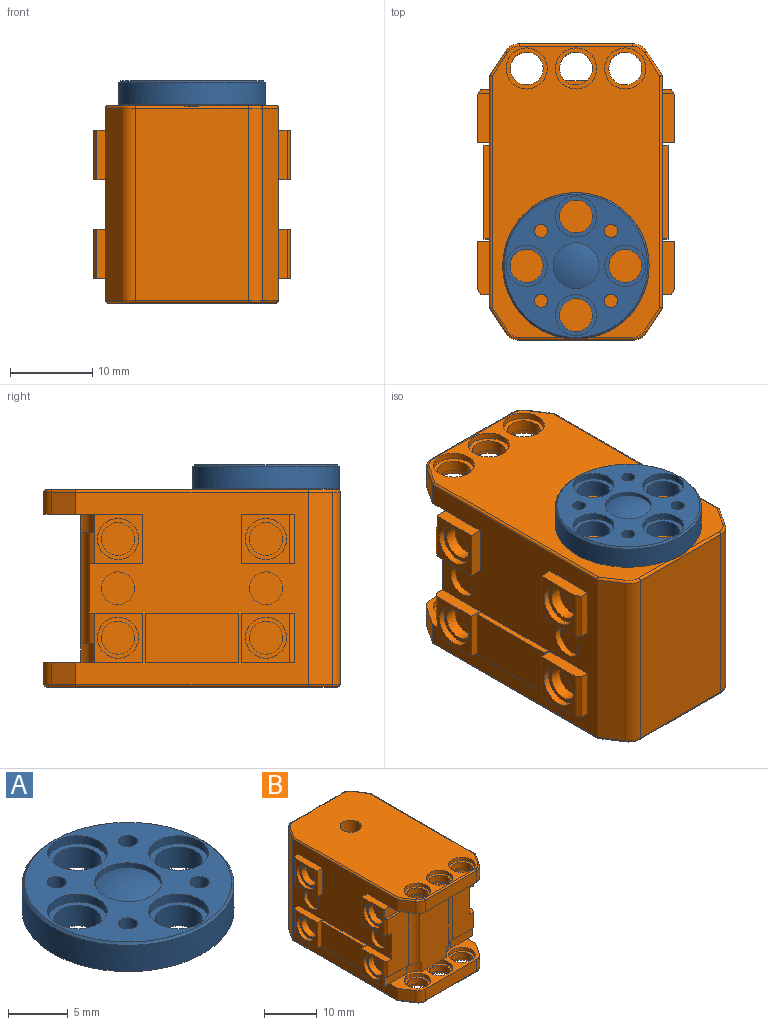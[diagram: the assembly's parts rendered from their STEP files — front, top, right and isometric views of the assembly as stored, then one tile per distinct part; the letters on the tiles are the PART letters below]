
ASSEMBLY  parts=2 mates=1
PART A: 22 faces, bbox 17.8x17.8x2.9 mm
  f0: revolved ~5.62x5.6mm, area 25.4mm2, adj f13
  f1: plane 5x5mm, normal (0,0,1), area 7.1mm2, adj f2,f3
  f2: cylinder r=2mm len=4mm, axis (0,0,1), area 26.4mm2, adj f1,f21
  f3: cylinder r=2.5mm len=5mm, axis (0,0,1), area 12.6mm2, adj f1,f19
  f4: plane 5x5mm, normal (0,0,1), area 7.1mm2, adj f5,f6
  f5: cylinder r=2mm len=4mm, axis (0,0,1), area 26.4mm2, adj f4,f21
  f6: cylinder r=2.5mm len=5mm, axis (0,0,1), area 12.6mm2, adj f4,f19
  f7: plane 5x5mm, normal (0,0,1), area 7.1mm2, adj f8,f9
  f8: cylinder r=2mm len=4mm, axis (0,0,1), area 26.4mm2, adj f7,f21
  f9: cylinder r=2.5mm len=5mm, axis (0,0,1), area 12.6mm2, adj f7,f19
  f10: plane 5x5mm, normal (0,0,1), area 7.1mm2, adj f11,f12
  f11: cylinder r=2mm len=4mm, axis (0,0,1), area 26.4mm2, adj f10,f21
  f12: cylinder r=2.5mm len=5mm, axis (0,0,1), area 12.6mm2, adj f10,f19
  f13: cylinder r=2.8mm len=5.6mm, axis (0,0,1), area 8.8mm2, adj f0,f19
  f14: cone r=8.9mm half-angle=45deg, axis (0,0,-1), area 15.6mm2, adj f15,f19
  f15: cylinder r=8.9mm len=17.8mm, axis (0,0,1), area 151mm2, adj f14,f21
  f16: cylinder r=0.8mm len=2.9mm, axis (0,0,1), area 14.6mm2, adj f19,f21
  f17: cylinder r=0.8mm len=2.9mm, axis (0,0,1), area 14.6mm2, adj f19,f21
  f18: cylinder r=0.8mm len=2.9mm, axis (0,0,1), area 14.6mm2, adj f19,f21
  f19: plane 17.4x17.4mm, normal (0,0,1), area 126.6mm2, adj f3,f6,f9,f12,f13,f14,f16,f17
  f20: cylinder r=0.8mm len=2.9mm, axis (0,0,1), area 14.6mm2, adj f19,f21
  f21: plane 17.8x17.8mm, normal (0,0,-1), area 190.5mm2, adj f2,f5,f8,f11,f15,f16,f17,f18
PART B: 203 faces, bbox 24x36x24 mm
  f0: cylinder r=8.9mm len=3.75mm, axis (0,0,1), area 0mm2, adj f1,f138
  f1: plane 35.6x20.4mm, normal (0,0,1), area 633.5mm2, adj f0,f38,f39,f40,f42,f43,f44,f61
  f2: plane 4x4mm, normal (1,0,0), area 12.6mm2, adj f10
  f3: plane 4x4mm, normal (1,0,0), area 12.6mm2, adj f11
  f4: plane 4x4mm, normal (1,0,0), area 12.6mm2, adj f12
  f5: plane 4x4mm, normal (1,0,0), area 12.6mm2, adj f13
  f6: plane 4x4mm, normal (-1,0,0), area 12.6mm2, adj f14
  f7: plane 4x4mm, normal (-1,0,0), area 12.6mm2, adj f15
  f8: plane 4x4mm, normal (-1,0,0), area 12.6mm2, adj f16
  f9: plane 4x4mm, normal (-1,0,0), area 12.6mm2, adj f17
  f10: cylinder r=2mm len=4mm, axis (1,0,0), area 17.6mm2, adj f2,f18
  f11: cylinder r=2mm len=4mm, axis (1,0,0), area 17.6mm2, adj f3,f19
  f12: cylinder r=2mm len=4mm, axis (1,0,0), area 17.6mm2, adj f4,f20
  f13: cylinder r=2mm len=4mm, axis (1,0,0), area 17.6mm2, adj f5,f21
  f14: cylinder r=2mm len=4mm, axis (1,0,0), area 17.6mm2, adj f6,f28
  f15: cylinder r=2mm len=4mm, axis (1,0,0), area 17.6mm2, adj f7,f29
  f16: cylinder r=2mm len=4mm, axis (1,0,0), area 17.6mm2, adj f8,f31
  f17: cylinder r=2mm len=4mm, axis (1,0,0), area 17.6mm2, adj f9,f32
  f18: plane 5x5mm, normal (1,0,0), area 7.1mm2, adj f10,f34
  f19: plane 5x5mm, normal (1,0,0), area 7.1mm2, adj f11,f35
  f20: plane 5x5mm, normal (1,0,0), area 7.1mm2, adj f12,f36
  f21: plane 5x5mm, normal (1,0,0), area 7.1mm2, adj f13,f37
  f22: plane 5x5mm, normal (0,0,1), area 7.1mm2, adj f26,f38
  f23: plane 5x5mm, normal (0,0,1), area 7.1mm2, adj f25,f39
  f24: plane 5x5mm, normal (0,0,1), area 7.1mm2, adj f27,f40
  f25: cylinder r=2mm len=4mm, axis (0,0,1), area 17.6mm2, adj f23,f41
  f26: cylinder r=2mm len=4mm, axis (0,0,1), area 17.6mm2, adj f22,f45
  f27: cylinder r=2mm len=4mm, axis (0,0,1), area 17.6mm2, adj f24,f46
  f28: plane 5x5mm, normal (-1,0,0), area 7.1mm2, adj f14,f47
  f29: plane 5x5mm, normal (-1,0,0), area 7.1mm2, adj f15,f48
  f30: plane 4x1mm, normal (0,0,1), area 2.8mm2, adj f49,f74
  f31: plane 5x5mm, normal (-1,0,0), area 7.1mm2, adj f16,f50
  f32: plane 5x5mm, normal (-1,0,0), area 7.1mm2, adj f17,f51
  f33: plane 4x1mm, normal (0,0,-1), area 2.8mm2, adj f49,f91
  f34: cylinder r=2.5mm len=5mm, axis (1,0,0), area 12.6mm2, adj f18,f54
  f35: cylinder r=2.5mm len=5mm, axis (1,0,0), area 12.6mm2, adj f19,f60
  f36: cylinder r=2.5mm len=5mm, axis (1,0,0), area 12.6mm2, adj f20,f63
  f37: cylinder r=2.5mm len=5mm, axis (1,0,0), area 12.6mm2, adj f21,f65
  f38: cylinder r=2.5mm len=5mm, axis (0,0,1), area 12.6mm2, adj f1,f22
  f39: cylinder r=2.5mm len=5mm, axis (0,0,1), area 12.6mm2, adj f1,f23
  f40: cylinder r=2.5mm len=5mm, axis (0,0,1), area 12.6mm2, adj f1,f24
  f41: plane 5x5mm, normal (0,0,-1), area 7.1mm2, adj f25,f74
  f42: revolved ~1.68x1.07mm, area 0.9mm2, adj f1,f43,f73,f77
  f43: cylinder r=0.3mm len=13.83mm, axis (1,0,0), area 6.5mm2, adj f1,f42,f44,f78
  f44: revolved ~1.68x1.07mm, area 0.9mm2, adj f1,f43,f61,f79
  f45: plane 5x5mm, normal (0,0,-1), area 7.1mm2, adj f26,f82
  f46: plane 5x5mm, normal (0,0,-1), area 7.1mm2, adj f27,f83
  f47: cylinder r=2.5mm len=5mm, axis (1,0,0), area 12.6mm2, adj f28,f84
  f48: cylinder r=2.5mm len=5mm, axis (1,0,0), area 12.6mm2, adj f29,f90
  f49: plane 18x8mm, normal (0,-1,0), area 138.4mm2, adj f30,f33,f56,f57,f58,f75,f81,f86
  f50: cylinder r=2.5mm len=5mm, axis (1,0,0), area 12.6mm2, adj f31,f99
  f51: cylinder r=2.5mm len=5mm, axis (1,0,0), area 12.6mm2, adj f32,f101
  f52: revolved ~1.68x1.07mm, area 0.9mm2, adj f111,f186,f187,f200
  f53: revolved ~1.68x1.07mm, area 0.9mm2, adj f112,f187,f188,f200
  f54: plane 6x5.84mm, normal (1,0,0), area 15.4mm2, adj f34,f59,f114,f115,f116
  f55: plane 6x0.66mm, normal (0.84,-0.54,0), area 3.3mm2, adj f56,f60,f80,f117,f118,f120
  f56: plane 8.54x1.53mm, normal (0,0,1), area 4.5mm2, adj f49,f55,f57,f80,f81,f117
  f57: cylinder r=2.5mm len=13.5mm, axis (0,0,1), area 31.3mm2, adj f49,f56,f58,f117
  f58: plane 8.54x1.53mm, normal (0,0,-1), area 4.5mm2, adj f49,f57,f59,f94,f95,f117
  f59: plane 6x0.66mm, normal (0.84,-0.54,0), area 3.3mm2, adj f54,f58,f94,f114,f116,f117
  f60: plane 6x5.84mm, normal (1,0,0), area 15.4mm2, adj f35,f55,f118,f119,f120
  f61: cylinder r=0.3mm len=3.1mm, axis (0.54,0.84,0), area 1.6mm2, adj f1,f44,f113,f121
  f62: plane 6x0.66mm, normal (0.84,0.54,0), area 4.7mm2, adj f63,f122,f123,f124
  f63: plane 6x5.84mm, normal (1,0,0), area 15.4mm2, adj f36,f62,f122,f124,f125
  f64: plane 6x0.66mm, normal (0.84,0.54,0), area 4.7mm2, adj f65,f126,f127,f128
  f65: plane 6x5.84mm, normal (1,0,0), area 15.4mm2, adj f37,f64,f126,f128,f129
  f66: plane 4x4mm, normal (1,0,0), area 12.6mm2, adj f130
  f67: plane 4x4mm, normal (1,0,0), area 12.6mm2, adj f131
  f68: plane 11.4x6mm, normal (1,0,0), area 68.4mm2, adj f132,f133,f134,f135
  f69: revolved ~1.68x1.07mm, area 0.9mm2, adj f137,f190,f191,f200
  f70: revolved ~1.68x1.07mm, area 0.9mm2, adj f1,f136,f137,f138
  f71: revolved ~1.68x1.07mm, area 0.9mm2, adj f139,f191,f192,f200
  f72: revolved ~1.68x1.07mm, area 0.9mm2, adj f1,f138,f139,f140
  f73: cylinder r=0.3mm len=3.1mm, axis (0.54,-0.84,0), area 1.6mm2, adj f1,f42,f141,f142
  f74: cylinder r=2.5mm len=5mm, axis (0,0,1), area 12.6mm2, adj f30,f41,f143
  f75: cylinder r=3.02mm len=2.63mm, axis (0,0,1), area 7.2mm2, adj f49,f76,f88,f143
  f76: plane 5.91x2.25mm, normal (0,-1,0), area 13.3mm2, adj f75,f88,f89,f143,f144
  f77: cylinder r=2mm len=2.7mm, axis (0,0,1), area 5.4mm2, adj f42,f78,f142,f143
  f78: plane 13.83x2.7mm, normal (0,-1,0), area 37.3mm2, adj f43,f77,f79,f143
  f79: cylinder r=2mm len=2.7mm, axis (0,0,1), area 5.4mm2, adj f44,f78,f121,f143
  f80: plane 5.91x2.25mm, normal (0,-1,0), area 13.3mm2, adj f55,f56,f81,f120,f143
  f81: cylinder r=3.02mm len=2.63mm, axis (0,0,1), area 7.2mm2, adj f49,f56,f80,f143
  f82: cylinder r=2.5mm len=5mm, axis (0,0,1), area 12.6mm2, adj f45,f143
  f83: cylinder r=2.5mm len=5mm, axis (0,0,1), area 12.6mm2, adj f46,f143
  f84: plane 6x5.84mm, normal (-1,0,0), area 15.4mm2, adj f47,f89,f144,f145,f146
  f85: plane 6x0.66mm, normal (-0.84,-0.54,0), area 3.3mm2, adj f86,f90,f93,f147,f148,f150
  f86: plane 8.54x1.53mm, normal (0,0,-1), area 4.5mm2, adj f49,f85,f87,f92,f93,f147
  f87: cylinder r=2.5mm len=13.5mm, axis (0,0,1), area 31.3mm2, adj f49,f86,f88,f147
  f88: plane 8.54x1.53mm, normal (0,0,1), area 4.5mm2, adj f49,f75,f76,f87,f89,f147
  f89: plane 6x0.66mm, normal (-0.84,-0.54,0), area 3.3mm2, adj f76,f84,f88,f144,f146,f147
  f90: plane 6x5.84mm, normal (-1,0,0), area 15.4mm2, adj f48,f85,f148,f149,f150
  f91: cylinder r=2.5mm len=5mm, axis (0,0,1), area 12.6mm2, adj f33,f109,f151
  f92: cylinder r=3.02mm len=2.63mm, axis (0,0,1), area 7.2mm2, adj f49,f86,f93,f151
  f93: plane 5.91x2.25mm, normal (0,-1,0), area 13.3mm2, adj f85,f86,f92,f150,f151
  f94: plane 5.91x2.25mm, normal (0,-1,0), area 13.3mm2, adj f58,f59,f95,f114,f151
  f95: cylinder r=3.02mm len=2.63mm, axis (0,0,1), area 7.2mm2, adj f49,f58,f94,f151
  f96: cylinder r=2.5mm len=5mm, axis (0,0,1), area 12.6mm2, adj f108,f151
  f97: cylinder r=2.5mm len=5mm, axis (0,0,1), area 12.6mm2, adj f110,f151
  f98: plane 6x0.66mm, normal (-0.84,0.54,0), area 4.7mm2, adj f99,f152,f153,f154
  f99: plane 6x5.84mm, normal (-1,0,0), area 15.4mm2, adj f50,f98,f152,f154,f155
  f100: plane 6x0.66mm, normal (-0.84,0.54,0), area 4.7mm2, adj f101,f156,f157,f158
  f101: plane 6x5.84mm, normal (-1,0,0), area 15.4mm2, adj f51,f100,f156,f158,f159
  f102: plane 4x4mm, normal (-1,0,0), area 12.6mm2, adj f160
  f103: plane 4x4mm, normal (-1,0,0), area 12.6mm2, adj f161
  f104: plane 11.4x6mm, normal (-1,0,0), area 68.4mm2, adj f162,f163,f164,f165
  f105: plane 4x4mm, normal (0,0,-1), area 12.6mm2, adj f166
  f106: plane 4x4mm, normal (0,0,-1), area 12.6mm2, adj f167
  f107: plane 4x4mm, normal (0,0,-1), area 12.6mm2, adj f168
  f108: plane 5x5mm, normal (0,0,1), area 7.1mm2, adj f96,f169
  f109: plane 5x5mm, normal (0,0,1), area 7.1mm2, adj f91,f170
  f110: plane 5x5mm, normal (0,0,1), area 7.1mm2, adj f97,f171
  f111: cylinder r=2mm len=2.7mm, axis (0,0,1), area 5.4mm2, adj f52,f151,f172,f173
  f112: cylinder r=2mm len=2.7mm, axis (0,0,1), area 5.4mm2, adj f53,f151,f173,f174
  f113: cylinder r=0.3mm len=28.3mm, axis (0,1,0), area 13.3mm2, adj f1,f61,f136,f175
  f114: plane 5.98x1.5mm, normal (0,0,-1), area 9mm2, adj f54,f59,f94,f115,f175
  f115: plane 6x1.5mm, normal (0,1,0), area 9mm2, adj f54,f114,f116,f175
  f116: plane 6.5x1.5mm, normal (0,0,1), area 9.6mm2, adj f54,f59,f115,f117,f175
  f117: plane 13.5x5.57mm, normal (0,-1,0), area 68.8mm2, adj f55,f56,f57,f58,f59,f116,f118,f175
  f118: plane 6.5x1.5mm, normal (0,0,-1), area 9.6mm2, adj f55,f60,f117,f119,f175
  f119: plane 6x1.5mm, normal (0,1,0), area 9mm2, adj f60,f118,f120,f175
  f120: plane 5.98x1.5mm, normal (0,0,1), area 9mm2, adj f55,f60,f80,f119,f175
  f121: plane 2.94x2.7mm, normal (0.84,-0.54,0), area 9.5mm2, adj f61,f79,f143,f175
  f122: plane 6.5x1.5mm, normal (0,0,-1), area 9.6mm2, adj f62,f63,f123,f125,f175
  f123: plane 6x1.07mm, normal (0,1,0), area 6.4mm2, adj f62,f122,f124,f175
  f124: plane 6.5x1.5mm, normal (0,0,1), area 9.6mm2, adj f62,f63,f123,f125,f175
  f125: plane 6x1.5mm, normal (0,-1,0), area 9mm2, adj f63,f122,f124,f175
  f126: plane 6.5x1.5mm, normal (0,0,-1), area 9.6mm2, adj f64,f65,f127,f129,f175
  f127: plane 6x1.07mm, normal (0,1,0), area 6.4mm2, adj f64,f126,f128,f175
  f128: plane 6.5x1.5mm, normal (0,0,1), area 9.6mm2, adj f64,f65,f127,f129,f175
  f129: plane 6x1.5mm, normal (0,-1,0), area 9mm2, adj f65,f126,f128,f175
  f130: cylinder r=2mm len=4mm, axis (1,0,0), area 10.1mm2, adj f66,f175
  f131: cylinder r=2mm len=4mm, axis (1,0,0), area 10.1mm2, adj f67,f175
  f132: plane 11.4x0.7mm, normal (0,0,1), area 8mm2, adj f68,f133,f135,f175
  f133: plane 6x0.7mm, normal (0,-1,0), area 4.2mm2, adj f68,f132,f134,f175
  f134: plane 11.4x0.7mm, normal (0,0,-1), area 8mm2, adj f68,f133,f135,f175
  f135: plane 6x0.7mm, normal (0,1,0), area 4.2mm2, adj f68,f132,f134,f175
  f136: cylinder r=0.3mm len=3.1mm, axis (-0.54,0.84,0), area 1.6mm2, adj f1,f70,f113,f176
  f137: cylinder r=2mm len=23.4mm, axis (0,0,-1), area 46.6mm2, adj f69,f70,f176,f177
  f138: cylinder r=0.3mm len=13.83mm, axis (-1,0,0), area 6mm2, adj f0,f1,f70,f72,f177
  f139: cylinder r=2mm len=23.4mm, axis (0,0,-1), area 46.6mm2, adj f71,f72,f177,f178
  f140: cylinder r=0.3mm len=3.1mm, axis (-0.54,-0.84,0), area 1.6mm2, adj f1,f72,f141,f178
  f141: cylinder r=0.3mm len=28.3mm, axis (0,-1,0), area 13.3mm2, adj f1,f73,f140,f179
  f142: plane 2.94x2.7mm, normal (-0.84,-0.54,0), area 9.5mm2, adj f73,f77,f143,f179
  f143: plane 21x6.03mm, normal (0,0,-1), area 47.8mm2, adj f49,f74,f75,f76,f77,f78,f79,f80
  f144: plane 5.98x1.5mm, normal (0,0,1), area 9mm2, adj f76,f84,f89,f145,f179
  f145: plane 6x1.5mm, normal (0,1,0), area 9mm2, adj f84,f144,f146,f179
  f146: plane 6.5x1.5mm, normal (0,0,-1), area 9.6mm2, adj f84,f89,f145,f147,f179
  f147: plane 13.5x5.57mm, normal (0,-1,0), area 68.8mm2, adj f85,f86,f87,f88,f89,f146,f148,f179
  f148: plane 6.5x1.5mm, normal (0,0,1), area 9.6mm2, adj f85,f90,f147,f149,f179
  f149: plane 6x1.5mm, normal (0,1,0), area 9mm2, adj f90,f148,f150,f179
  f150: plane 5.98x1.5mm, normal (0,0,-1), area 9mm2, adj f85,f90,f93,f149,f179
  f151: plane 21x6.03mm, normal (0,0,1), area 47.8mm2, adj f49,f91,f92,f93,f94,f95,f96,f97
  f152: plane 6.5x1.5mm, normal (0,0,1), area 9.6mm2, adj f98,f99,f153,f155,f179
  f153: plane 6x1.07mm, normal (0,1,0), area 6.4mm2, adj f98,f152,f154,f179
  f154: plane 6.5x1.5mm, normal (0,0,-1), area 9.6mm2, adj f98,f99,f153,f155,f179
  f155: plane 6x1.5mm, normal (0,-1,0), area 9mm2, adj f99,f152,f154,f179
  f156: plane 6.5x1.5mm, normal (0,0,1), area 9.6mm2, adj f100,f101,f157,f159,f179
  f157: plane 6x1.07mm, normal (0,1,0), area 6.4mm2, adj f100,f156,f158,f179
  f158: plane 6.5x1.5mm, normal (0,0,-1), area 9.6mm2, adj f100,f101,f157,f159,f179
  f159: plane 6x1.5mm, normal (0,-1,0), area 9mm2, adj f101,f156,f158,f179
  f160: cylinder r=2mm len=4mm, axis (1,0,0), area 10.1mm2, adj f102,f179
  f161: cylinder r=2mm len=4mm, axis (1,0,0), area 10.1mm2, adj f103,f179
  f162: plane 11.4x0.7mm, normal (0,0,1), area 8mm2, adj f104,f163,f165,f179
  f163: plane 6x0.7mm, normal (0,1,0), area 4.2mm2, adj f104,f162,f164,f179
  f164: plane 11.4x0.7mm, normal (0,0,-1), area 8mm2, adj f104,f163,f165,f179
  f165: plane 6x0.7mm, normal (0,-1,0), area 4.2mm2, adj f104,f162,f164,f179
  f166: cylinder r=2mm len=4mm, axis (0,0,-1), area 27.6mm2, adj f105,f180
  f167: cylinder r=2mm len=4mm, axis (0,0,-1), area 27.6mm2, adj f106,f181
  f168: cylinder r=2mm len=4mm, axis (0,0,-1), area 27.6mm2, adj f107,f182
  f169: cylinder r=2mm len=4mm, axis (0,0,1), area 17.6mm2, adj f108,f183
  f170: cylinder r=2mm len=4mm, axis (0,0,1), area 17.6mm2, adj f109,f184
  f171: cylinder r=2mm len=4mm, axis (0,0,1), area 17.6mm2, adj f110,f185
  f172: plane 2.94x2.7mm, normal (-0.84,-0.54,0), area 9.5mm2, adj f111,f151,f179,f186
  f173: plane 13.83x2.7mm, normal (0,-1,0), area 37.3mm2, adj f111,f112,f151,f187
  f174: plane 2.94x2.7mm, normal (0.84,-0.54,0), area 9.5mm2, adj f112,f151,f175,f188
  f175: plane 28.3x23.4mm, normal (1,0,0), area 383mm2, adj f113,f114,f115,f116,f117,f118,f119,f120
  f176: plane 23.4x2.94mm, normal (0.84,0.54,0), area 82mm2, adj f136,f137,f175,f190
  f177: plane 23.4x13.83mm, normal (0,1,0), area 323.6mm2, adj f137,f138,f139,f191
  f178: plane 23.4x2.94mm, normal (-0.84,0.54,0), area 82mm2, adj f139,f140,f179,f192
  f179: plane 28.3x23.4mm, normal (-1,0,0), area 383mm2, adj f141,f142,f143,f144,f145,f146,f147,f148
  f180: plane 5x5mm, normal (0,0,-1), area 7.1mm2, adj f166,f194
  f181: plane 5x5mm, normal (0,0,-1), area 7.1mm2, adj f167,f195
  f182: plane 5x5mm, normal (0,0,-1), area 7.1mm2, adj f168,f196
  f183: plane 5x5mm, normal (0,0,-1), area 7.1mm2, adj f169,f197
  f184: plane 5x5mm, normal (0,0,-1), area 7.1mm2, adj f170,f198
  f185: plane 5x5mm, normal (0,0,-1), area 7.1mm2, adj f171,f199
  f186: cylinder r=0.3mm len=3.1mm, axis (-0.54,0.84,0), area 1.6mm2, adj f52,f172,f193,f200
  f187: cylinder r=0.3mm len=13.83mm, axis (-1,0,0), area 6.5mm2, adj f52,f53,f173,f200
  f188: cylinder r=0.3mm len=3.1mm, axis (-0.54,-0.84,0), area 1.6mm2, adj f53,f174,f189,f200
  f189: cylinder r=0.3mm len=28.3mm, axis (0,-1,0), area 13.3mm2, adj f175,f188,f190,f200
  f190: cylinder r=0.3mm len=3.1mm, axis (0.54,-0.84,0), area 1.6mm2, adj f69,f176,f189,f200
  f191: cylinder r=0.3mm len=13.83mm, axis (1,0,0), area 6.5mm2, adj f69,f71,f177,f200
  f192: cylinder r=0.3mm len=3.1mm, axis (0.54,0.84,0), area 1.6mm2, adj f71,f178,f193,f200
  f193: cylinder r=0.3mm len=28.3mm, axis (0,1,0), area 13.3mm2, adj f179,f186,f192,f200
  f194: cylinder r=2.5mm len=5mm, axis (0,0,-1), area 12.6mm2, adj f180,f200
  f195: cylinder r=2.5mm len=5mm, axis (0,0,-1), area 12.6mm2, adj f181,f200
  f196: cylinder r=2.5mm len=5mm, axis (0,0,-1), area 12.6mm2, adj f182,f200
  f197: cylinder r=2.5mm len=5mm, axis (0,0,-1), area 12.6mm2, adj f183,f200
  f198: cylinder r=2.5mm len=5mm, axis (0,0,-1), area 12.6mm2, adj f184,f200
  f199: cylinder r=2.5mm len=5mm, axis (0,0,-1), area 12.6mm2, adj f185,f200
  f200: plane 35.4x20.4mm, normal (0,0,-1), area 586.6mm2, adj f52,f53,f69,f71,f186,f187,f188,f189
  f201: cylinder r=2mm len=5mm, axis (0,0,1), area 62.8mm2, adj f1,f202
  f202: plane 4x4mm, normal (0,0,1), area 12.6mm2, adj f201
PLACE A t=(0,0,12)mm
PLACE B rot(axis=(0,0,1),180deg) t=(0,0,12)mm
MATE revolute A.f13 <-> B.f0  axis (0,0,-1) through (0,0,24)mm
